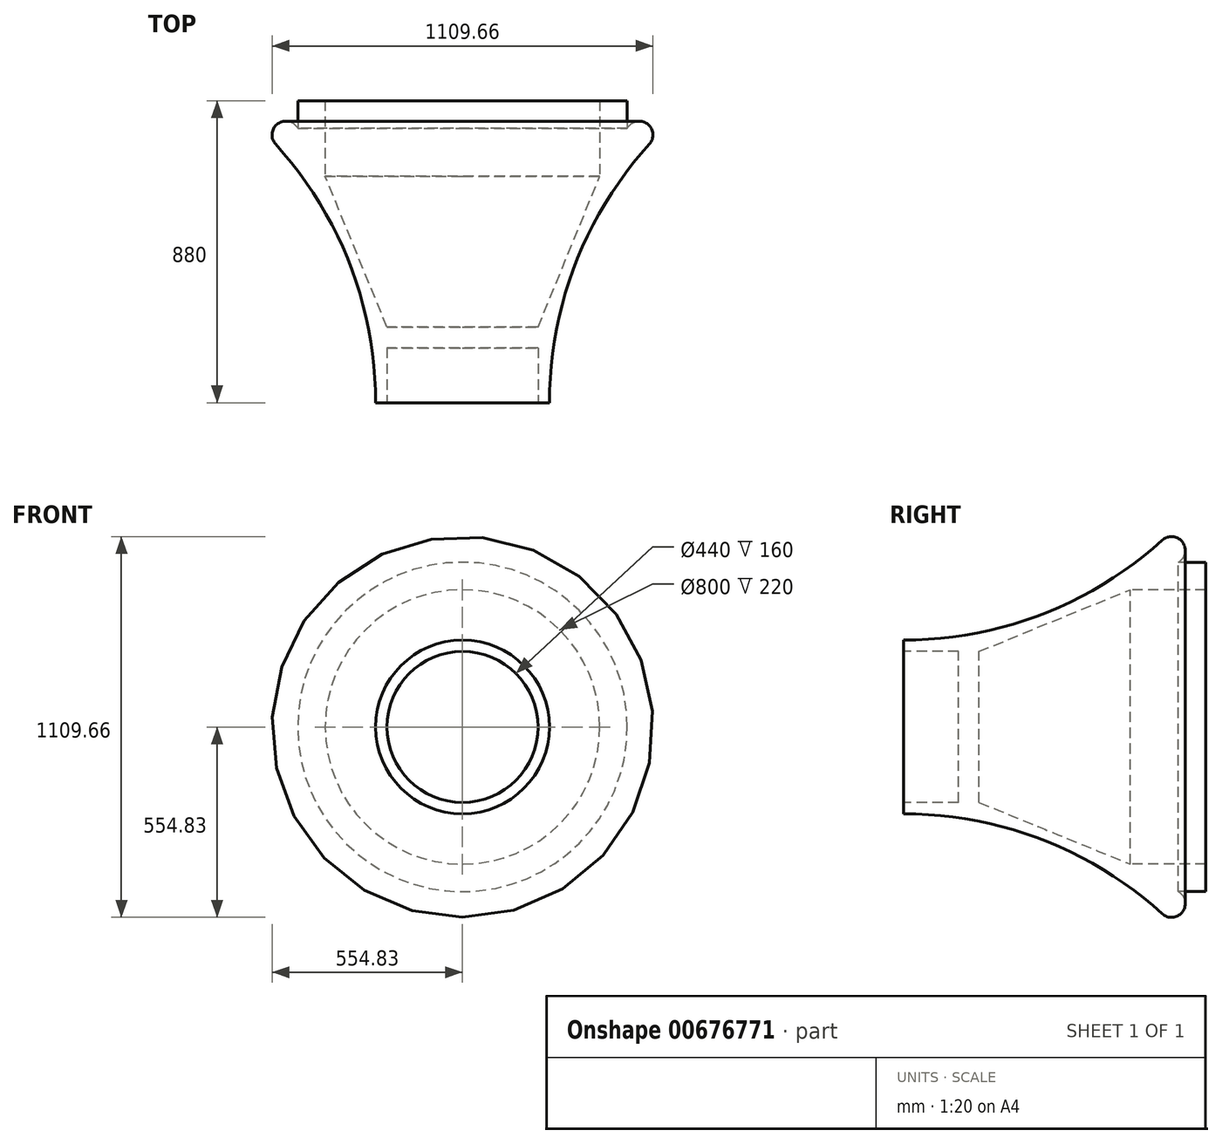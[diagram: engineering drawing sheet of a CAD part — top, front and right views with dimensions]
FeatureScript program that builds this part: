
annotation { "Feature Type Name" : "Feature", "Feature Type Description" : "" }
export const myFeature = defineFeature(function(context is Context, id is Id, definition is map)
    precondition{}
    {
        {
            var Q0;
            Q0=qCreatedBy(makeId("Top.planeOp"),FACE);
            var sketch = newSketch(context, id + "F0", { "sketchPlane" : qUnion([Q0])});
            skLineSegment(sketch, "E0", {"start": v(220, -157.94) * mm, "end": v(253.13, -157.94) * mm});
            skLineSegment(sketch, "E1", {"start": v(0, 40.82) * mm, "end": v(0, 62.06) * mm});
            skArc(sketch, "E2", {"start": v(544.43, 595.49) * mm, "mid": v(328.5, 245.95) * mm, "end": v(253.13, -157.94) * mm});
            skPoint(sketch, "E3.start.orphan", {"position": v(0, -63.63) * mm});
            skLineSegment(sketch, "E4", {"start": v(0, 2.06) * mm, "end": v(0, 62.06) * mm});
            skCircle(sketch, "E5", {"center": v(514.83, 622.4) * mm, "radius": 40 * mm});
            skLineSegment(sketch, "E6", {"start": v(400, 722.06) * mm, "end": v(480, 722.06) * mm});
            skLineSegment(sketch, "E7", {"start": v(480, 722.06) * mm, "end": v(480, 642.06) * mm});
            skLineSegment(sketch, "E8", {"start": v(400, 722.06) * mm, "end": v(400, 502.06) * mm});
            skLineSegment(sketch, "E9", {"start": v(220, -157.94) * mm, "end": v(220, 2.06) * mm});
            skLineSegment(sketch, "E10", {"start": v(220, 2.06) * mm, "end": v(0, 2.06) * mm});
            skLineSegment(sketch, "E11", {"start": v(0, 62.06) * mm, "end": v(220, 62.06) * mm});
            skLineSegment(sketch, "E12", {"start": v(220, 62.06) * mm, "end": v(400, 502.06) * mm});
            skPoint(sketch, "E13.orphan", {"position": v(813.13, -157.94) * mm});
            skPoint(sketch, "E14.orphan", {"position": v(0, -157.94) * mm});
            skPoint(sketch, "E15.start.orphan", {"position": v(0, 722.06) * mm});
            skSolve(sketch);
        }
        {
            var Q0;
            Q0 = qSketchRegion(id + "F0", true);
            var Q1;
            Q1=sQuery(id+"F0.wireOp",EDGE,"E4");
            revolve(context, id + "F1", {"entities" : qUnion([Q0]), "axis" : qUnion([Q1]), "revolveType" : RevolveType.FULL});
        }
    });
